# Revit family: Shower_Set-American_Standard-Traditional-1660.628_Series
name_source: partatom
category: Plumbing Fixtures
revit_build: Autodesk Revit 2015 (Build: 20140606_1530(x64)
units: mm (PartAtom-declared; Revit-internal decimal feet)

## types (2) — shared parameters
Assembly Code = D2010710
CW Connection = Yes
CWFU = 1
Cold Water Connection Diameter = 1/2"
Cold Water Connection Radius = 1/4"
Default Elevation = 44"
Description = Traditional 5-Function Hand Shower System Kit
Flow Rate = 1.5 gpm/5.7 lpm
HW Connection = Yes
HWFU = 2
Height = 23 5/8"
Hot Water Connection Diameter = 1"
Hot Water Connection Radius = 1/4"
Installation Type = Wall-Mounted
Manufacturer = American Standard
Price = Prices may vary. Please consult Manufacturer Representative for most up-to-date price list.
Product Documentation Link = https://www.americanstandard-us.com
Product Page URL = https://www.americanstandard-us.com
URL = https://www.americanstandard-us.com
Vent Connection = No
WFU = 2
Warranty Information = Limited 1-Year Warranty
Waste Connection = No
Width = 5"

## per-type parameters (varying)
| type | Finish | Material |
| 1660.628.002 | Brass-American Standard-002-Polished Chrome | Metal-American Standard-002-Chrome Plated |
| 1660.628.295 | Metal-American Standard-295-PVF Satin Nickel | Metal-American Standard-295-PVF Satin Nickel |

note: column(s) folded — value = type name in every type: Model

## geometry (parser evidence)
native form markers: Sweep x3
no freeform markers — native parametric forms only
